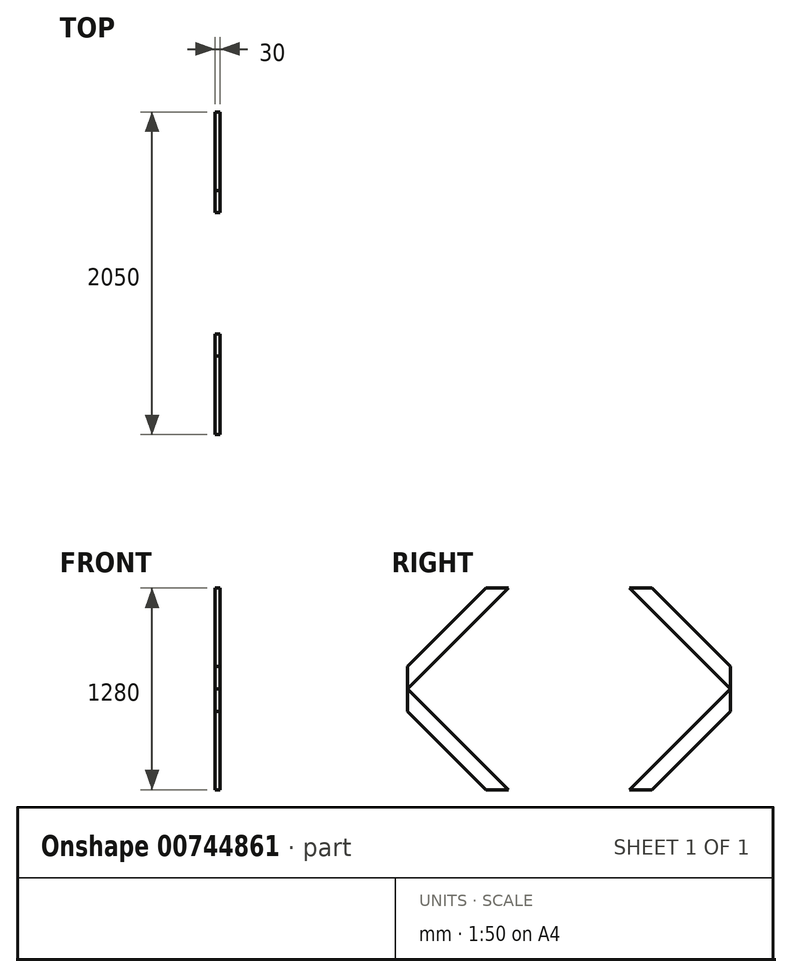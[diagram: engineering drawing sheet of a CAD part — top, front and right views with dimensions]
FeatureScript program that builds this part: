
annotation { "Feature Type Name" : "Feature", "Feature Type Description" : "" }
export const myFeature = defineFeature(function(context is Context, id is Id, definition is map)
    precondition{}
    {
        {
            var Q0;
            Q0=qCreatedBy(makeId("Right.planeOp"),FACE);
            var sketch = newSketch(context, id + "F0", { "sketchPlane" : qUnion([Q0])});
            skLineSegment(sketch, "E0", {"start": v(0, 498.58) * mm, "end": v(0, 498.58) * mm});
            skLineSegment(sketch, "E1", {"start": v(0, 498.58) * mm, "end": v(498.58, 0) * mm});
            skLineSegment(sketch, "E2", {"start": v(0, 640) * mm, "end": v(640, 0) * mm});
            skLineSegment(sketch, "E3", {"start": v(1025, 1280) * mm, "end": v(1025, 0) * mm, "construction": true});
            skLineSegment(sketch, "E4", {"start": v(0, 640) * mm, "end": v(2050, 640) * mm, "construction": true});
            skLineSegment(sketch, "E5", {"start": v(498.58, 0) * mm, "end": v(640, 0) * mm});
            skLineSegment(sketch, "E6", {"start": v(0, 640) * mm, "end": v(0, 498.58) * mm});
            skLineSegment(sketch, "E7.MirrorCS", {"start": v(0, 640) * mm, "end": v(640, 1280) * mm});
            skLineSegment(sketch, "E8.MirrorCS", {"start": v(498.58, 1280) * mm, "end": v(640, 1280) * mm});
            skLineSegment(sketch, "E9.MirrorCS", {"start": v(0, 781.42) * mm, "end": v(498.58, 1280) * mm});
            skLineSegment(sketch, "E10.MirrorCS", {"start": v(0, 640) * mm, "end": v(0, 781.42) * mm});
            skLineSegment(sketch, "E11.MirrorCS", {"start": v(1551.42, 1280) * mm, "end": v(1410, 1280) * mm});
            skLineSegment(sketch, "E12.MirrorCS", {"start": v(2050, 781.42) * mm, "end": v(1551.42, 1280) * mm});
            skLineSegment(sketch, "E13.MirrorCS", {"start": v(2050, 640) * mm, "end": v(1410, 1280) * mm});
            skLineSegment(sketch, "E14.MirrorCS", {"start": v(2050, 640) * mm, "end": v(2050, 781.42) * mm});
            skLineSegment(sketch, "E15.MirrorCS", {"start": v(2050, 640) * mm, "end": v(1410, 0) * mm});
            skLineSegment(sketch, "E16.MirrorCS", {"start": v(2050, 640) * mm, "end": v(2050, 498.58) * mm});
            skLineSegment(sketch, "E17.MirrorCS", {"start": v(2050, 498.58) * mm, "end": v(1551.42, 0) * mm});
            skLineSegment(sketch, "E18.MirrorCS", {"start": v(1551.42, 0) * mm, "end": v(1410, 0) * mm});
            skSolve(sketch);
        }
        {
            var Q0;
            Q0=makeQuery(id+"F0.imprint","IMPRINT",FACE,{"disambiguationData":[TD([[makeQuery(id+"F0.imprint","IMPRINT",EDGE,{"derivedFrom":sQuery(id+"F0.wireOp",EDGE,"E7.MirrorCS")}),1.0]])]});
            var Q1;
            Q1=makeQuery(id+"F0.imprint","IMPRINT",FACE,{"disambiguationData":[TD([[makeQuery(id+"F0.imprint","IMPRINT",EDGE,{"derivedFrom":sQuery(id+"F0.wireOp",EDGE,"E1")}),1.0]])]});
            var Q2;
            Q2=makeQuery(id+"F0.imprint","IMPRINT",FACE,{"disambiguationData":[TD([[makeQuery(id+"F0.imprint","IMPRINT",EDGE,{"derivedFrom":sQuery(id+"F0.wireOp",EDGE,"E15.MirrorCS")}),1.0]])]});
            var Q3;
            Q3=makeQuery(id+"F0.imprint","IMPRINT",FACE,{"disambiguationData":[TD([[makeQuery(id+"F0.imprint","IMPRINT",EDGE,{"derivedFrom":sQuery(id+"F0.wireOp",EDGE,"E11.MirrorCS")}),1.0]])]});
            extrude(context, id + "F1", {"entities" : qUnion([Q0, Q1, Q2, Q3]), "depth" : 30 * mm, "offsetDistance" : 25 * mm});
        }
    });
